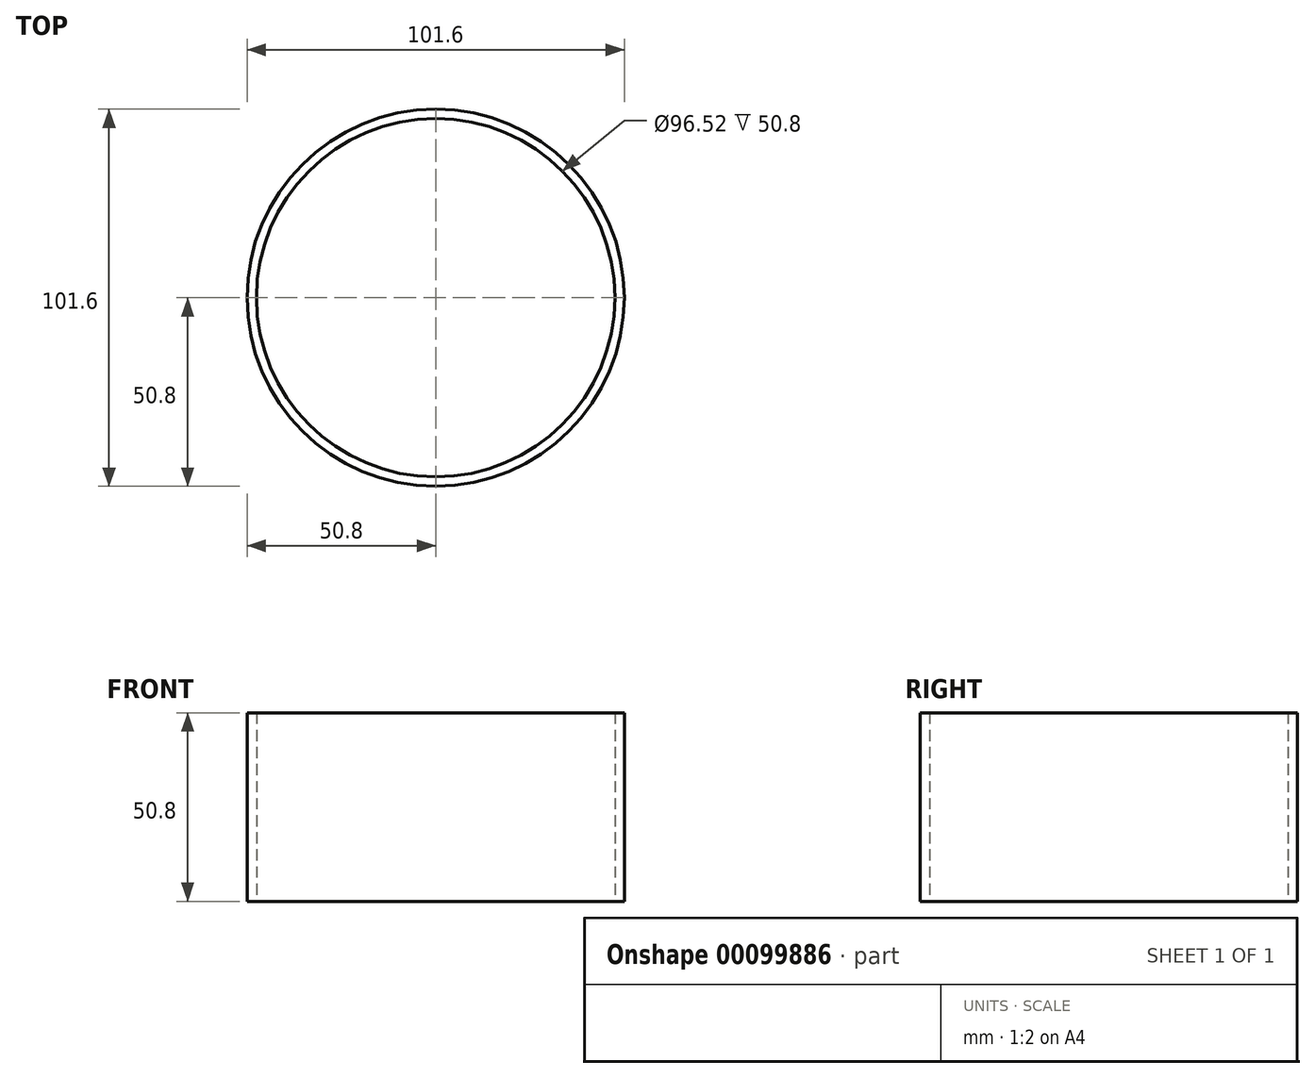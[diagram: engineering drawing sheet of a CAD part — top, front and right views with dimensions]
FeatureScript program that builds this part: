
annotation { "Feature Type Name" : "Feature", "Feature Type Description" : "" }
export const myFeature = defineFeature(function(context is Context, id is Id, definition is map)
    precondition{}
    {
        {
            var Q0;
            Q0=qCreatedBy(makeId("Top.planeOp"),FACE);
            var sketch = newSketch(context, id + "F0", { "sketchPlane" : qUnion([Q0])});
            skCircle(sketch, "E0", {"center": v(0, 0) * mm, "radius": 50.8 * mm});
            skSolve(sketch);
        }
        {
            var Q0;
            Q0 = qSketchRegion(id + "F0", true);
            extrude(context, id + "F1", {"entities" : qUnion([Q0]), "endBound" : BoundingType.SYMMETRIC, "depth" : 50.8 * mm});
        }
        {
            var Q0;
            Q0=makeQuery(id+"F1.opExtrude","CAP_FACE",FACE,{"disambiguationData":[OSD([sQuery(id+"F0.wireOp",EDGE,"E0")])],"isStart":true});
            var Q1;
            Q1=makeQuery(id+"F1.opExtrude","CAP_FACE",FACE,{"disambiguationData":[OSD([sQuery(id+"F0.wireOp",EDGE,"E0")])],"isStart":false});
            shell(context, id + "F2", {"entities" : qUnion([Q0, Q1]), "thickness" : 2.54 * mm});
        }
    });
